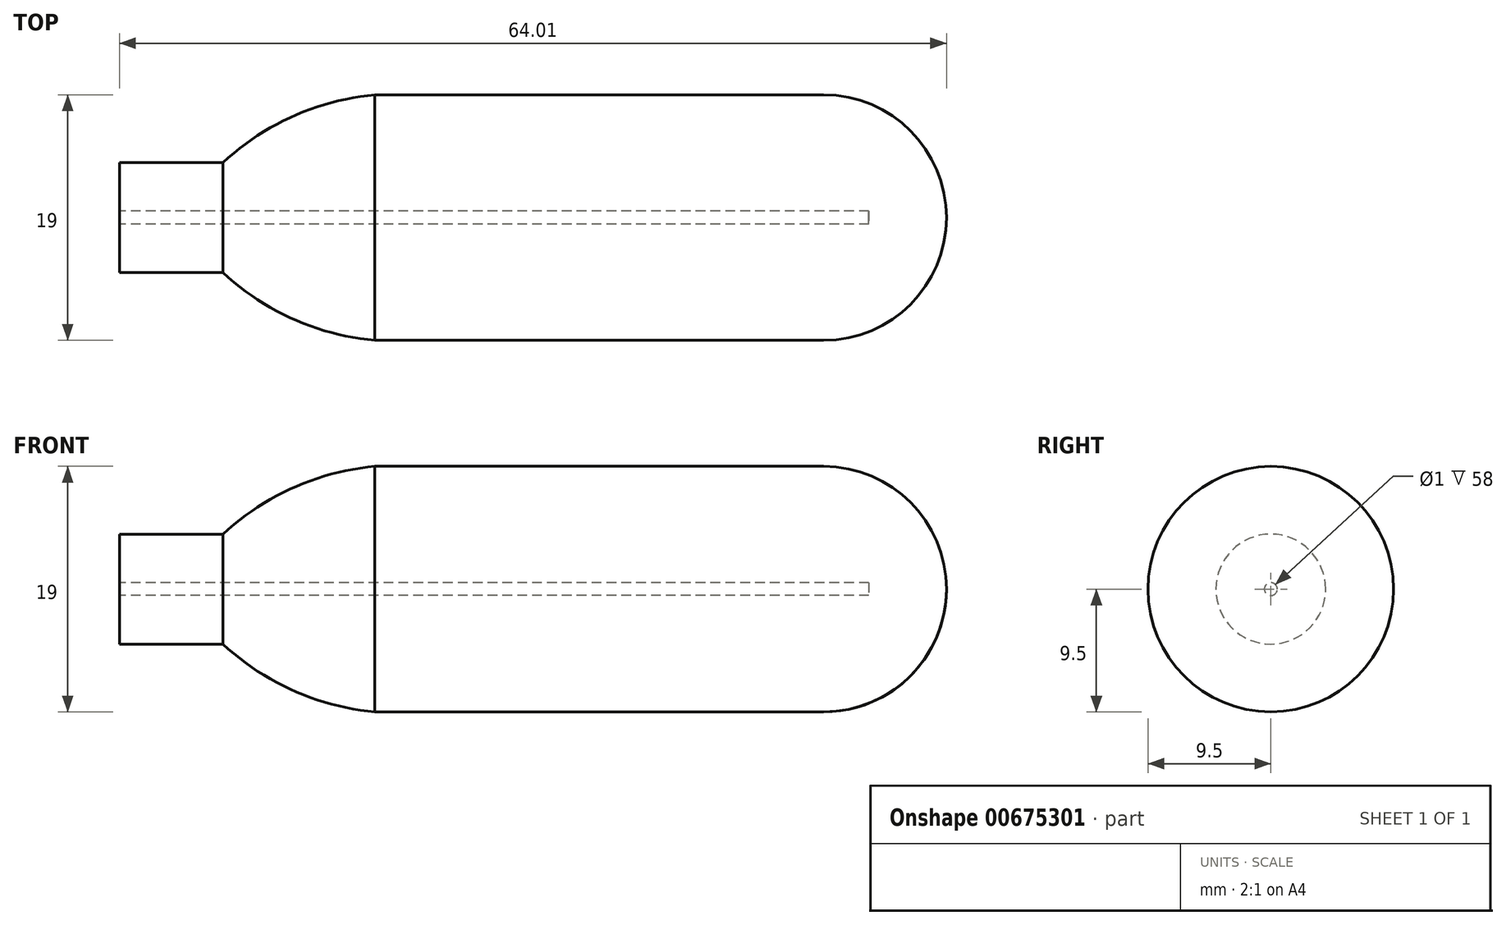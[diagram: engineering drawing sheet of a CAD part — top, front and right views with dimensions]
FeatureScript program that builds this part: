
annotation { "Feature Type Name" : "Feature", "Feature Type Description" : "" }
export const myFeature = defineFeature(function(context is Context, id is Id, definition is map)
    precondition{}
    {
        {
            var Q0;
            Q0=qCreatedBy(makeId("Front.planeOp"),FACE);
            var sketch = newSketch(context, id + "F0", { "sketchPlane" : qUnion([Q0])});
            skLineSegment(sketch, "E0", {"start": v(0, 0) * mm, "end": v(8, 0) * mm});
            skLineSegment(sketch, "E1", {"start": v(0, 0) * mm, "end": v(0, 4.25) * mm});
            skLineSegment(sketch, "E2", {"start": v(0, 4.25) * mm, "end": v(8, 4.25) * mm});
            skLineSegment(sketch, "E3", {"start": v(0, 0) * mm, "end": v(64, 0) * mm});
            skLineSegment(sketch, "E4", {"start": v(19.78, 9.5) * mm, "end": v(32, 9.5) * mm});
            skLineSegment(sketch, "E5", {"start": v(32, 9.5) * mm, "end": v(47.55, 9.5) * mm});
            skArc(sketch, "E6", {"start": v(19.78, 9.5) * mm, "mid": v(13.45, 7.85) * mm, "end": v(8, 4.25) * mm});
            skPoint(sketch, "E7.end.orphan", {"position": v(7.55, 9.5) * mm});
            skLineSegment(sketch, "E8", {"start": v(19.78, 9.5) * mm, "end": v(47.55, 9.5) * mm});
            skLineSegment(sketch, "E9", {"start": v(47.55, 9.5) * mm, "end": v(64, 9.5) * mm});
            skLineSegment(sketch, "E10", {"start": v(64, 9.5) * mm, "end": v(64, 0) * mm});
            skSolve(sketch);
        }
        {
            var Q0;
            {var subQ1=sQuery(id+"F0.wireOp",EDGE,"E1");Q0=makeQuery(id+"F0.imprint","IMPRINT",FACE,{"disambiguationData":[TD([[makeQuery(id+"F0.imprint","IMPRINT",EDGE,{"derivedFrom":subQ1}),-1.0]])]});}
            var Q1;
            Q1=sQuery(id+"F0.wireOp",EDGE,"E3");
            revolve(context, id + "F1", {"entities" : qUnion([Q0]), "axis" : qUnion([Q1]), "revolveType" : RevolveType.FULL});
        }
        {
            var Q0;
            Q0=makeQuery(id+"F1.opRevolve","SWEPT_EDGE",EDGE,{"disambiguationData":[OSD([sQuery(id+"F0.wireOp",EDGE,"E9"),sQuery(id+"F0.wireOp",EDGE,"E10")])]});
            fillet(context, id + "F2", {"entities" : qUnion([Q0]), "radius" : 9.5 * mm, "tangentPropagation" : true, "allowEdgeOverflow" : false});
        }
        {
            var Q0;
            Q0=makeQuery(id+"F1.opRevolve","SWEPT_FACE",FACE,{"disambiguationData":[OSD([sQuery(id+"F0.wireOp",EDGE,"E1")])]});
            var sketch = newSketch(context, id + "F3", { "sketchPlane" : qUnion([Q0])});
            skCircle(sketch, "E11", {"center": v(0, 0) * mm, "radius": 0.5 * mm});
            skSolve(sketch);
        }
        {
            var Q0;
            Q0 = qSketchRegion(id + "F3", true);
            extrude(context, id + "F4", {"entities" : qUnion([Q0]), "operationType" : NewBodyOperationType.REMOVE, "oppositeDirection" : true, "depth" : 58 * mm, "offsetDistance" : 25 * mm});
        }
    });
